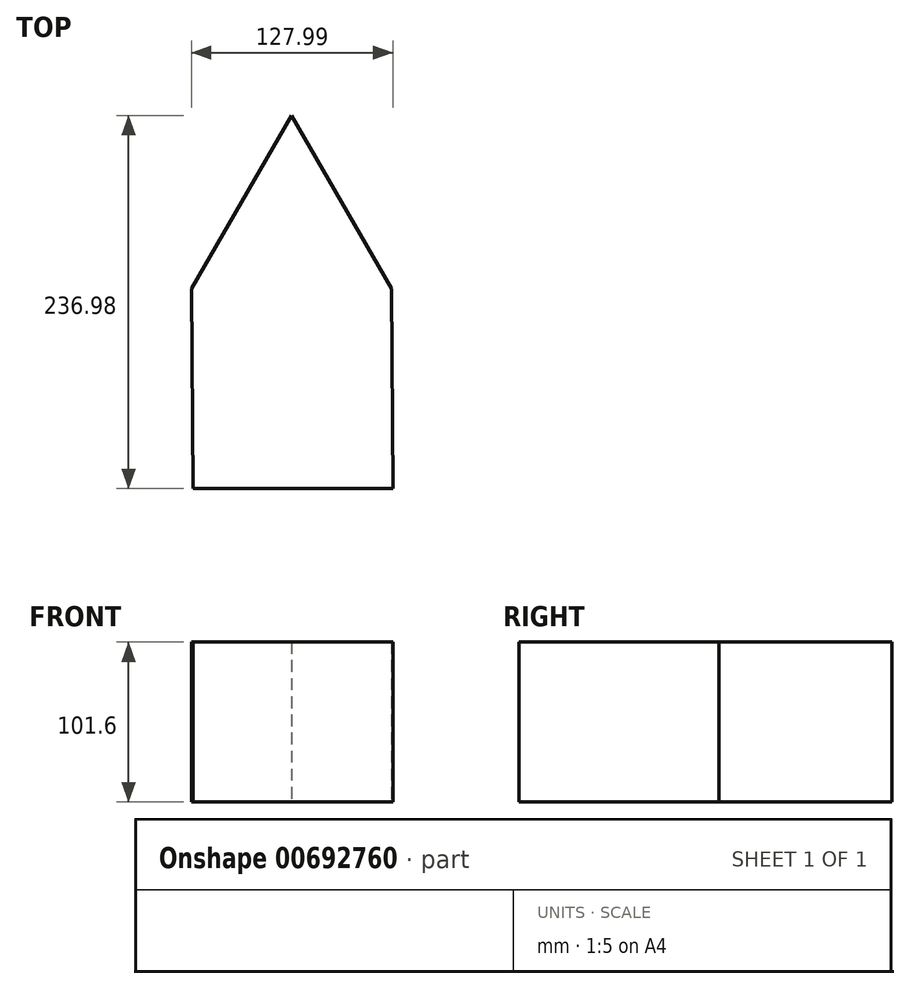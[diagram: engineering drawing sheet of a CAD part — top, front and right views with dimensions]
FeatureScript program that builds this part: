
annotation { "Feature Type Name" : "Feature", "Feature Type Description" : "" }
export const myFeature = defineFeature(function(context is Context, id is Id, definition is map)
    precondition{}
    {
        {
            var Q0;
            Q0=qCreatedBy(makeId("Top.planeOp"),FACE);
            var sketch = newSketch(context, id + "F0", { "sketchPlane" : qUnion([Q0])});
            skLineSegment(sketch, "E0.bottom", {"start": v(-83.44, -73.46) * mm, "end": v(43.56, -73.46) * mm});
            skLineSegment(sketch, "E0.left", {"start": v(-83.44, -73.46) * mm, "end": v(-84.43, 53.53) * mm});
            skLineSegment(sketch, "E0.right", {"start": v(43.56, -73.46) * mm, "end": v(42.57, 53.53) * mm});
            skLineSegment(sketch, "E1", {"start": v(-84.43, 53.53) * mm, "end": v(-20.93, 163.52) * mm});
            skLineSegment(sketch, "E2", {"start": v(-20.93, 163.52) * mm, "end": v(42.57, 53.53) * mm});
            skSolve(sketch);
        }
        {
            var Q0;
            Q0 = qSketchRegion(id + "F0", true);
            extrude(context, id + "F1", {"entities" : qUnion([Q0]), "depth" : 101.6 * mm, "offsetDistance" : 25.4 * mm});
        }
    });
